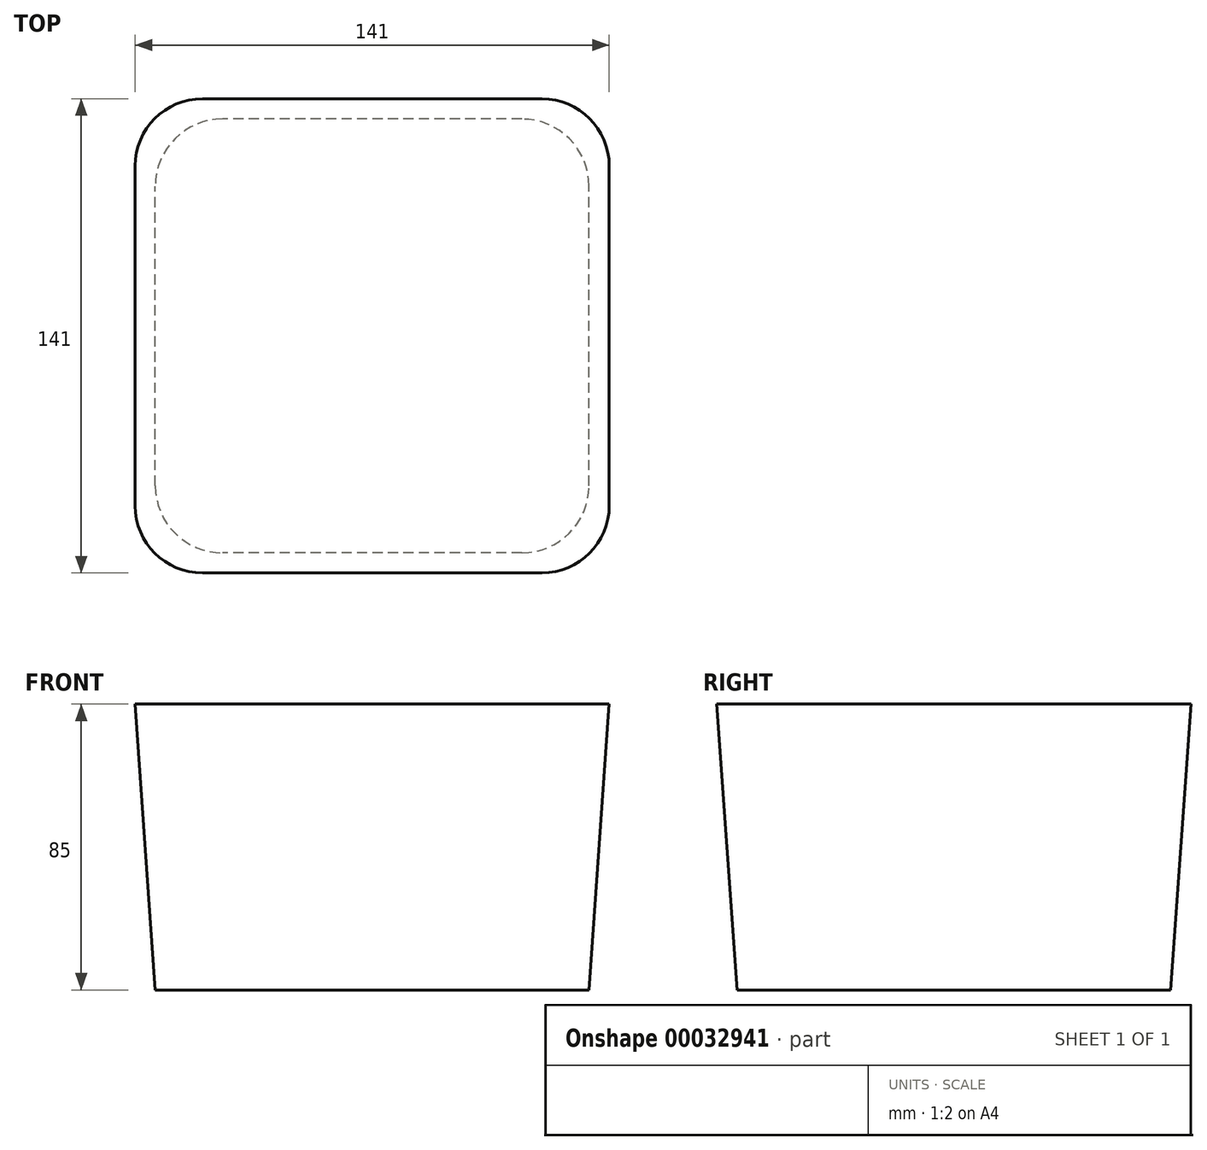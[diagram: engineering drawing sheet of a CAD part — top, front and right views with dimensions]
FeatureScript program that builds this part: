
annotation { "Feature Type Name" : "Feature", "Feature Type Description" : "" }
export const myFeature = defineFeature(function(context is Context, id is Id, definition is map)
    precondition{}
    {
        {
            var Q0;
            Q0=qCreatedBy(makeId("Top.planeOp"),FACE);
            var sketch = newSketch(context, id + "F0", { "sketchPlane" : qUnion([Q0])});
            skLineSegment(sketch, "E0.rect.bottom", {"start": v(44.5, -64.5) * mm, "end": v(-44.5, -64.5) * mm});
            skLineSegment(sketch, "E0.rect.top", {"start": v(44.5, 64.5) * mm, "end": v(-44.5, 64.5) * mm});
            skLineSegment(sketch, "E0.rect.left", {"start": v(64.5, -44.5) * mm, "end": v(64.5, 44.5) * mm});
            skLineSegment(sketch, "E0.rect.right", {"start": v(-64.5, -44.5) * mm, "end": v(-64.5, 44.5) * mm});
            skPoint(sketch, "E0.rect.middle", {"position": v(0, 0) * mm});
            skPoint(sketch, "E1.visualSharp", {"position": v(-64.5, 64.5) * mm});
            skArc(sketch, "E1.filletArc", {"start": v(-44.5, 64.5) * mm, "mid": v(-58.64, 58.64) * mm, "end": v(-64.5, 44.5) * mm});
            skPoint(sketch, "E2.visualSharp", {"position": v(64.5, 64.5) * mm});
            skArc(sketch, "E2.filletArc", {"start": v(64.5, 44.5) * mm, "mid": v(58.64, 58.64) * mm, "end": v(44.5, 64.5) * mm});
            skPoint(sketch, "E3.visualSharp", {"position": v(64.5, -64.5) * mm});
            skArc(sketch, "E3.filletArc", {"start": v(44.5, -64.5) * mm, "mid": v(58.64, -58.64) * mm, "end": v(64.5, -44.5) * mm});
            skPoint(sketch, "E4.visualSharp", {"position": v(-64.5, -64.5) * mm});
            skArc(sketch, "E4.filletArc", {"start": v(-64.5, -44.5) * mm, "mid": v(-58.64, -58.64) * mm, "end": v(-44.5, -64.5) * mm});
            skSolve(sketch);
        }
        {
            var Q0;
            Q0=makeQuery(id+"F0.imprint","IMPRINT",FACE,{"disambiguationData":[TD([[makeQuery(id+"F0.imprint","IMPRINT",EDGE,{"derivedFrom":sQuery(id+"F0.wireOp",EDGE,"E0.rect.bottom")}),-1.0]])]});
            cPlane(context, id + "F1", {"entities" : qUnion([Q0]), "cplaneType" : CPlaneType.OFFSET, "offset" : 85 * mm, "width" : 150 * mm, "height" : 150 * mm});
        }
        {
            var Q0;
            Q0=qCreatedBy(id+"F1.planeOp",FACE);
            var sketch = newSketch(context, id + "F2", { "sketchPlane" : qUnion([Q0])});
            skLineSegment(sketch, "E5.rect.bottom", {"start": v(50.5, 70.5) * mm, "end": v(-50.5, 70.5) * mm});
            skLineSegment(sketch, "E5.rect.top", {"start": v(50.5, -70.5) * mm, "end": v(-50.5, -70.5) * mm});
            skLineSegment(sketch, "E5.rect.left", {"start": v(70.5, 50.5) * mm, "end": v(70.5, -50.5) * mm});
            skLineSegment(sketch, "E5.rect.right", {"start": v(-70.5, 50.5) * mm, "end": v(-70.5, -50.5) * mm});
            skPoint(sketch, "E5.rect.middle", {"position": v(0, 0) * mm});
            skPoint(sketch, "E6.visualSharp", {"position": v(-70.5, -70.5) * mm});
            skArc(sketch, "E6.filletArc", {"start": v(-70.5, -50.5) * mm, "mid": v(-64.64, -64.64) * mm, "end": v(-50.5, -70.5) * mm});
            skPoint(sketch, "E7.visualSharp", {"position": v(70.5, -70.5) * mm});
            skArc(sketch, "E7.filletArc", {"start": v(50.5, -70.5) * mm, "mid": v(64.64, -64.64) * mm, "end": v(70.5, -50.5) * mm});
            skPoint(sketch, "E8.visualSharp", {"position": v(70.5, 70.5) * mm});
            skArc(sketch, "E8.filletArc", {"start": v(70.5, 50.5) * mm, "mid": v(64.64, 64.64) * mm, "end": v(50.5, 70.5) * mm});
            skPoint(sketch, "E9.visualSharp", {"position": v(-70.5, 70.5) * mm});
            skArc(sketch, "E9.filletArc", {"start": v(-50.5, 70.5) * mm, "mid": v(-64.64, 64.64) * mm, "end": v(-70.5, 50.5) * mm});
            skSolve(sketch);
        }
        {
            var Q0;
            Q0=makeQuery(id+"F0.imprint","IMPRINT",FACE,{"disambiguationData":[TD([[makeQuery(id+"F0.imprint","IMPRINT",EDGE,{"derivedFrom":sQuery(id+"F0.wireOp",EDGE,"E0.rect.bottom")}),-1.0]])]});
            var Q1;
            Q1=makeQuery(id+"F2.imprint","IMPRINT",FACE,{"disambiguationData":[TD([[makeQuery(id+"F2.imprint","IMPRINT",EDGE,{"derivedFrom":sQuery(id+"F2.wireOp",EDGE,"E5.rect.bottom")}),1.0]])]});
            loft(context, id + "F3", {"sheetProfilesArray" : [{ "sheetProfileEntities" : qUnion([Q0]) }, { "sheetProfileEntities" : qUnion([Q1]) }]});
        }
    });
